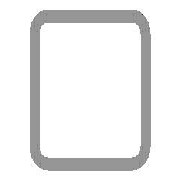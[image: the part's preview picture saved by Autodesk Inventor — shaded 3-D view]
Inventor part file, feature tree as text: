
AUTODESK INVENTOR PART (.ipt)
format: ipt  version: 2025 (Build 290162010, 162A)  size: 134,656 bytes
history: native  units: mm (DEFAULTED — no unit token found)
features: other x4, sketch x1, plane x1
ambient origin geometry x8: Origin, YZ Plane, XZ Plane, XY Plane, X Axis, Y Axis, Z Axis, Center Point
bodies: Solid1 (feature_tree), Body (feature_tree)
feature tree (6):
  parser-record x1  (decoder bookkeeping rows leaked as tree rows — omitted from the tree; the rows remain in map.json)
  other  "Driven Length"
  other  "Start Plane"
  other  "End Plane"
  sketch  "Sketch3"  dims[d3=546.129918mm d4=0.0mm d7=6.0mm d9=60.0mm d11=60.0mm d12=3.0mm d13=100.0mm d14=646.129918mm d15=30.0mm d16=30.0mm d17=90.0deg d18=546.129918mm]
  plane  "Work Plane3"
